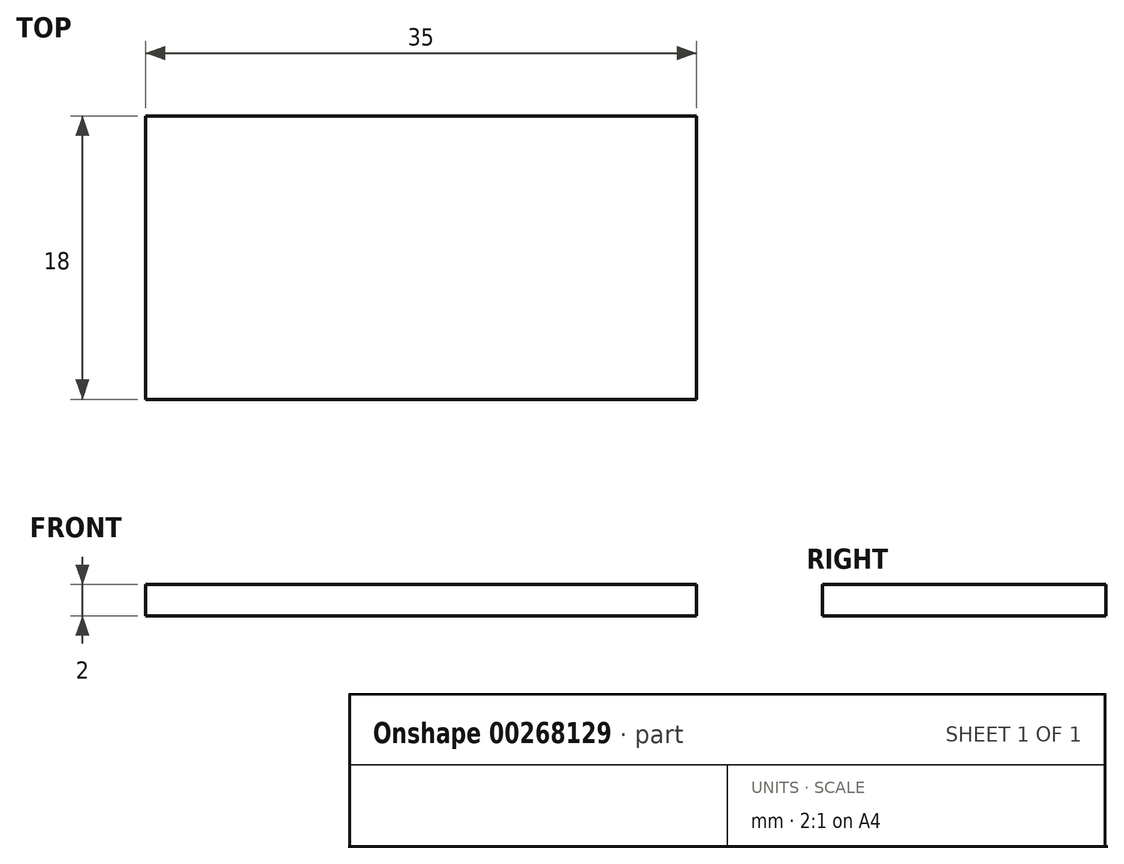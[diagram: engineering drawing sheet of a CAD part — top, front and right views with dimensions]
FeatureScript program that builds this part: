
annotation { "Feature Type Name" : "Feature", "Feature Type Description" : "" }
export const myFeature = defineFeature(function(context is Context, id is Id, definition is map)
    precondition{}
    {
        {
            var Q0;
            Q0=qCreatedBy(makeId("Top.planeOp"),FACE);
            var sketch = newSketch(context, id + "F0", { "sketchPlane" : qUnion([Q0])});
            skLineSegment(sketch, "E0.bottom", {"start": v(-17.5, 9) * mm, "end": v(17.5, 9) * mm});
            skLineSegment(sketch, "E0.top", {"start": v(-17.5, -9) * mm, "end": v(17.5, -9) * mm});
            skLineSegment(sketch, "E0.left", {"start": v(-17.5, 9) * mm, "end": v(-17.5, -9) * mm});
            skLineSegment(sketch, "E0.right", {"start": v(17.5, 9) * mm, "end": v(17.5, -9) * mm});
            skPoint(sketch, "E0.middle", {"position": v(0, 0) * mm});
            skSolve(sketch);
        }
        {
            var Q0;
            Q0 = qSketchRegion(id + "F0", true);
            extrude(context, id + "F1", {"entities" : qUnion([Q0]), "depth" : 2 * mm, "offsetDistance" : 25 * mm});
        }
    });
